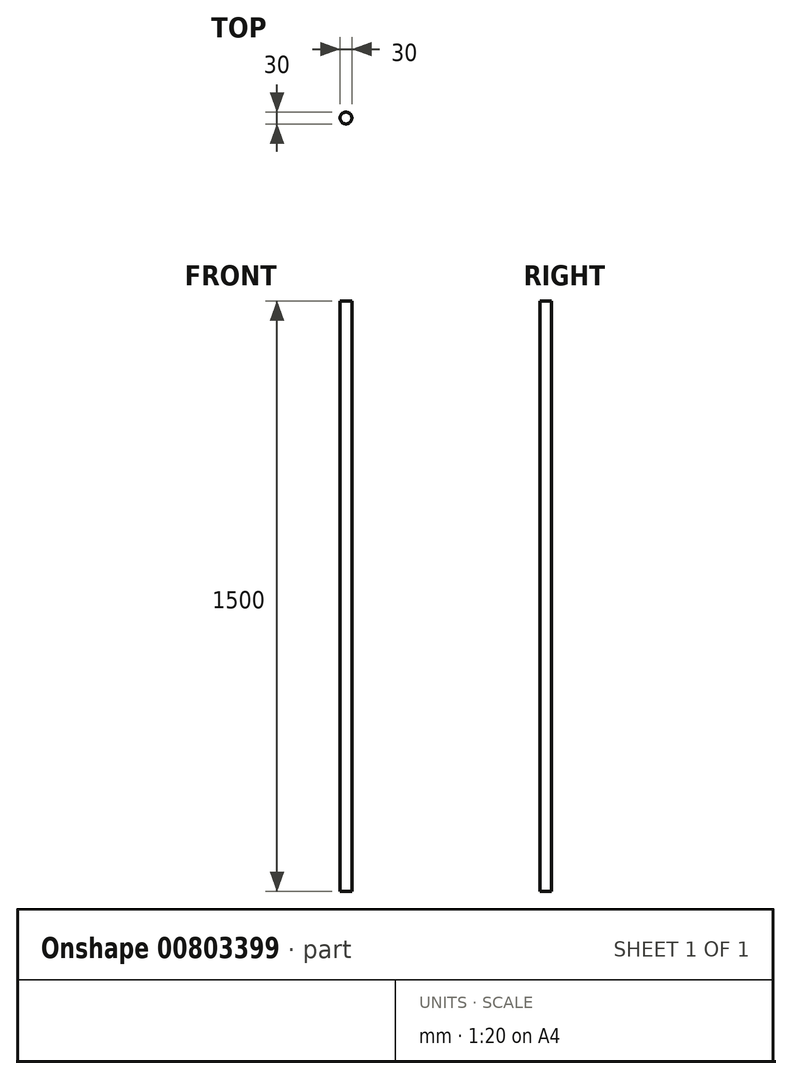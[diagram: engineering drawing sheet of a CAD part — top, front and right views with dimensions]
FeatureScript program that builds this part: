
annotation { "Feature Type Name" : "Feature", "Feature Type Description" : "" }
export const myFeature = defineFeature(function(context is Context, id is Id, definition is map)
    precondition{}
    {
        {
            var Q0;
            Q0=qCreatedBy(makeId("Top.planeOp"),FACE);
            var sketch = newSketch(context, id + "F0", { "sketchPlane" : qUnion([Q0])});
            skCircle(sketch, "E0", {"center": v(0, 0) * mm, "radius": 15 * mm});
            skSolve(sketch);
        }
        {
            var Q0;
            Q0=makeQuery(id+"F0.imprint","IMPRINT",FACE,{"disambiguationData":[TD([[makeQuery(id+"F0.imprint","IMPRINT",EDGE,{"derivedFrom":sQuery(id+"F0.wireOp",EDGE,"E0")}),1.0]])]});
            extrude(context, id + "F1", {"entities" : qUnion([Q0]), "depth" : 1500 * mm, "offsetDistance" : 25 * mm});
        }
    });
